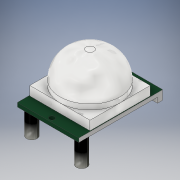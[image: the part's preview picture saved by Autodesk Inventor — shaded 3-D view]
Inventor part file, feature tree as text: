
AUTODESK INVENTOR PART (.ipt)
format: ipt  version: 2017.2 (Build 212223000, 223)  size: 240,128 bytes
history: native  units: in
note: dims shown in document units (in); Inventor stores cm internally (conversion verified against a paired STEP export)
features: sketch x8, extrude x7, fillet x1, hole x1
ambient origin geometry x8: Origin, YZ Plane, XZ Plane, XY Plane, X Axis, Y Axis, Z Axis, Center Point
bodies: Solid1 (feature_tree)
feature tree (17):
  extrude  "Extrusion1"  Depth=1.2598in
  extrude  "Extrusion2"  Depth=0.9055in
  extrude  "Extrusion3"  Depth=0.1378in TaperAngle=0.0deg
  fillet  "Fillet1"  Radius=0.9055in
  sketch  "Sketch4"  dims[d9=0.4724in d10=0.0in d11=0.3937in]
  extrude  "Extrusion4"  Depth=0.3937in
  extrude  "Extrusion5"  Depth=0.1575in
  extrude  "Extrusion6"  Depth=0.0787in
  extrude  "Extrusion7"  Depth=0.0787in
  hole  "Hole1"  [1 undecoded]
  sketch  "Sketch1"  dims[d0=0.9252in d1=1.2598in]
  sketch  "Sketch2"  dims[d2=0.0591in d3=0.0in d4=0.9055in]
  sketch  "Sketch3"  dims[d5=0.9055in d6=0.1378in d7=0.0in d8=0.9055in]
  sketch  "Sketch5"  dims[d13=0.1575in d14=0.1575in]
  sketch  "Sketch6"  dims[d16=0.2756in d17=0.0787in]
  sketch  "Sketch7"  dims[d18=0.0787in d19=0.0in d20=0.1575in]
  sketch  "Sketch8"  dims[d21=0.2756in d22=0.0787in d23=0.0787in d24=0.0in d26=0.1575in d27=0.1575in d28=0.1575in d29=0.3937in d30=0.0in d31=0.0197in d32=0.0197in d33=0.0197in d34=0.315in d35=0.0in d36=0.0197in d37=0.0787in d38=0.0787in d42=0.0787in d43=0.75in d44=0.375in d45=0.25in d46=0.5635in d47=1.0in d48=0.8108in]
note: 1 required parameter value undecoded (feature->parameter linkage not recoverable at this tier; creation-order binding heuristic only, values carry confidence <= 0.55)
